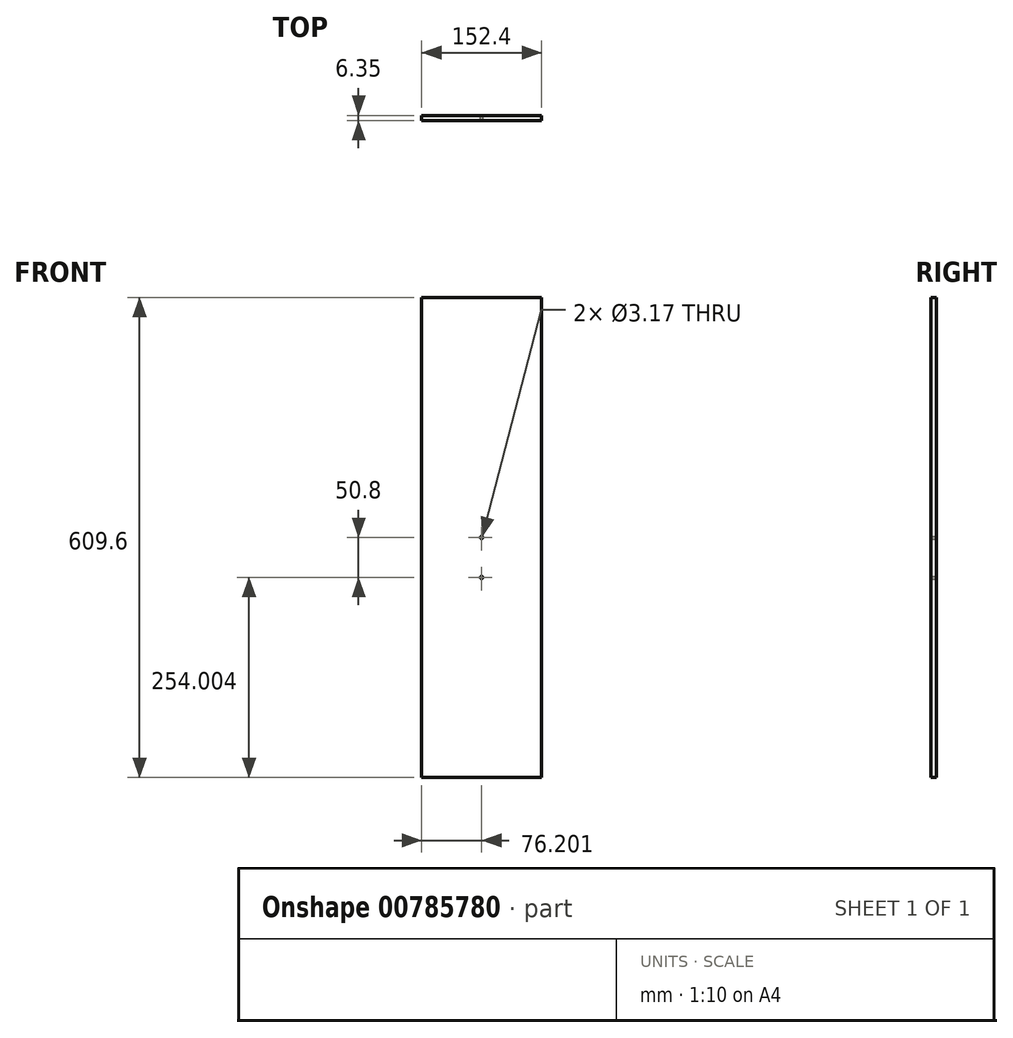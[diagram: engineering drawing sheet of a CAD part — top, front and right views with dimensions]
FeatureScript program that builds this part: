
annotation { "Feature Type Name" : "Feature", "Feature Type Description" : "" }
export const myFeature = defineFeature(function(context is Context, id is Id, definition is map)
    precondition{}
    {
        {
            var Q0;
            Q0=qCreatedBy(makeId("Front.planeOp"),FACE);
            var sketch = newSketch(context, id + "F0", { "sketchPlane" : qUnion([Q0])});
            skLineSegment(sketch, "E0.bottom", {"start": v(-115.38, 436.43) * mm, "end": v(37.02, 436.43) * mm});
            skLineSegment(sketch, "E0.top", {"start": v(-115.38, -173.17) * mm, "end": v(37.02, -173.17) * mm});
            skLineSegment(sketch, "E0.left", {"start": v(-115.38, 436.43) * mm, "end": v(-115.38, -173.17) * mm});
            skLineSegment(sketch, "E0.right", {"start": v(37.02, 436.43) * mm, "end": v(37.02, -173.17) * mm});
            skLineSegment(sketch, "E1", {"start": v(-39.18, -173.17) * mm, "end": v(-39.18, -97.07) * mm, "construction": true});
            skPoint(sketch, "E2", {"position": v(-39.18, 131.63) * mm});
            skPoint(sketch, "E3", {"position": v(-39.18, 80.83) * mm});
            skSolve(sketch);
        }
        {
            var Q0;
            Q0=makeQuery(id+"F0.imprint","IMPRINT",FACE,{"disambiguationData":[TD([[makeQuery(id+"F0.imprint","IMPRINT",EDGE,{"derivedFrom":sQuery(id+"F0.wireOp",EDGE,"E0.bottom")}),-1.0]])]});
            extrude(context, id + "F1", {"entities" : qUnion([Q0]), "depth" : 6.35 * mm, "offsetDistance" : 25.4 * mm});
        }
        {
            var Q0;
            Q0=sQuery(id+"F0.wireOp",VERTEX,"E2");
            var Q1;
            Q1=sQuery(id+"F0.wireOp",VERTEX,"E3");
            var Q2;
            Q2=makeQuery(id+"F1.opExtrude","SWEPT_BODY",BODY,{"disambiguationData":[OSD([sQuery(id+"F0.wireOp",EDGE,"E0.bottom"),sQuery(id+"F0.wireOp",EDGE,"E0.top"),sQuery(id+"F0.wireOp",EDGE,"E0.left"),sQuery(id+"F0.wireOp",EDGE,"E0.right")])]});
            hole(context, id + "F2", {"style" : HoleStyle.SIMPLE, "endStyle" : HoleEndStyle.THROUGH, "oppositeDirection" : true, "holeDiameter" : 3.17 * mm, "majorDiameter" : 6.35 * mm, "isTappedThrough" : true, "tappedDepth" : 12.7 * mm, "tapClearance" : 3, "locations" : qUnion([Q0, Q1]), "scope" : qUnion([Q2])});
        }
    });
